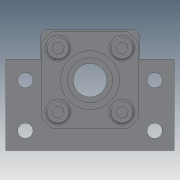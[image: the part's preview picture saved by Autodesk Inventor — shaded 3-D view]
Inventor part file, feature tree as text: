
AUTODESK INVENTOR PART (.ipt)
format: ipt  version: 2016 SP1 (Build 200210100, 210)  size: 374,784 bytes
history: native  units: in
note: dims shown in document units (in); Inventor stores cm internally (conversion verified against a paired STEP export)
features: extrude x9, sketch x5, other x2
ambient origin geometry x8: Origin, YZ Plane, XZ Plane, XY Plane, X Axis, Y Axis, Z Axis, Center Point
bodies: Body1 (feature_tree)
feature tree (16):
  other  "Твердое тело1"
  other  "bk-12"
  sketch  "Эскиз1"
  extrude  "Выдавливание1"  Depth=0.3937in TaperAngle=0.0deg
  extrude  "Выдавливание2"  Depth=0.3937in TaperAngle=0.0deg
  extrude  "Выдавливание3"  Depth=0.6299in
  extrude  "Выдавливание4"  Depth=0.9449in
  extrude  "Выдавливание5"  Depth=0.0394in TaperAngle=0.0deg
  extrude  "Выдавливание6"  Depth=0.0197in TaperAngle=0.0deg
  sketch  "Эскиз4"
  extrude  "Выдавливание7"  Depth=0.1575in TaperAngle=0.0deg
  extrude  "Выдавливание9"  Depth=0.0394in TaperAngle=0.0deg
  extrude  "Выдавливание8"  Depth=0.8268in
  sketch  "Эскиз2"
  sketch  "Эскиз3"
  sketch  "Эскиз5"
